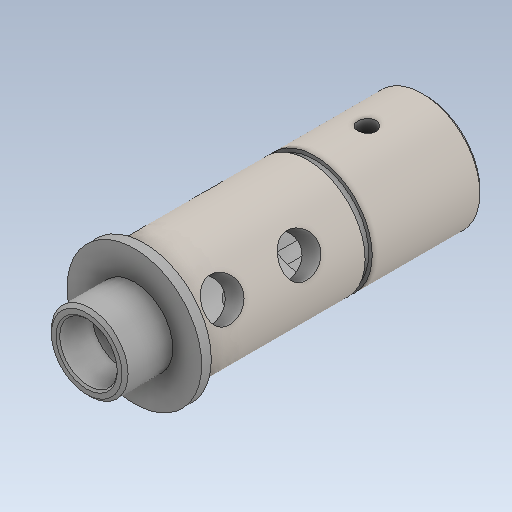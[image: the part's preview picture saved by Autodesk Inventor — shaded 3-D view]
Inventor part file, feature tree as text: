
AUTODESK INVENTOR PART (.ipt)
format: ipt  version: 2020 (Build 240168000, 168)  size: 229,888 bytes
history: native  units: in
note: dims shown in document units (in); Inventor stores cm internally (conversion verified against a paired STEP export)
features: chamfer x1
ambient origin geometry x8: Origin, YZ Plane, XZ Plane, XY Plane, X Axis, Y Axis, Z Axis, Center Point
bodies: Solid1 (feature_tree)
feature tree (1):
  chamfer  "Chamfer4"  [1 undecoded]
note: 1 required parameter value undecoded (feature->parameter linkage not recoverable at this tier; creation-order binding heuristic only, values carry confidence <= 0.55)
